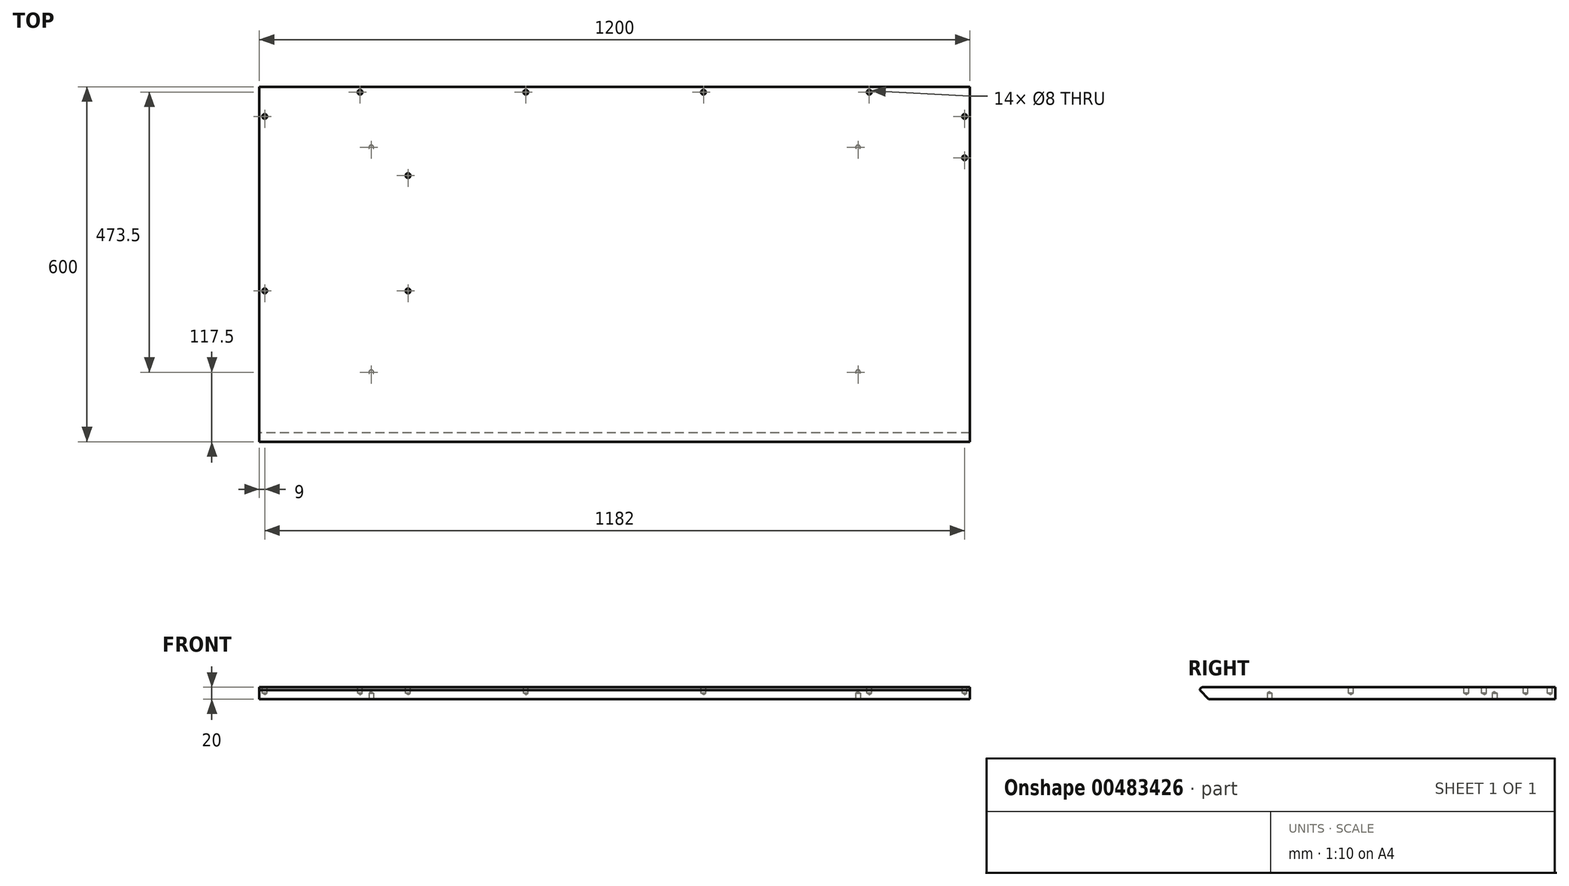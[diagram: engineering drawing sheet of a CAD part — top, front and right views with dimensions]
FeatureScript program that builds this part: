
annotation { "Feature Type Name" : "Feature", "Feature Type Description" : "" }
export const myFeature = defineFeature(function(context is Context, id is Id, definition is map)
    precondition{}
    {
        {
            var Q0;
            Q0=qCreatedBy(makeId("Top.planeOp"),FACE);
            var sketch = newSketch(context, id + "F0", { "sketchPlane" : qUnion([Q0])});
            skLineSegment(sketch, "E0.bottom", {"start": v(0, 0) * mm, "end": v(1200, 0) * mm});
            skLineSegment(sketch, "E0.top", {"start": v(0, -600) * mm, "end": v(1200, -600) * mm});
            skLineSegment(sketch, "E0.left", {"start": v(0, 0) * mm, "end": v(0, -600) * mm});
            skLineSegment(sketch, "E0.right", {"start": v(1200, 0) * mm, "end": v(1200, -600) * mm});
            skSolve(sketch);
        }
        {
            var Q0;
            Q0=makeQuery(id+"F0.imprint","IMPRINT",FACE,{"disambiguationData":[TD([[makeQuery(id+"F0.imprint","IMPRINT",EDGE,{"derivedFrom":sQuery(id+"F0.wireOp",EDGE,"E0.bottom")}),-1.0]])]});
            extrude(context, id + "F1", {"entities" : qUnion([Q0]), "depth" : 20 * mm});
        }
        {
            var Q0;
            Q0=makeQuery(id+"F1.opExtrude","CAP_EDGE",EDGE,{"disambiguationData":[OSD([sQuery(id+"F0.wireOp",EDGE,"E0.top")])],"isStart":false});
            fillet(context, id + "F2", {"entities" : qUnion([Q0]), "radius" : 5 * mm, "tangentPropagation" : true, "allowEdgeOverflow" : false});
        }
        {
            var Q0;
            Q0=makeQuery(id+"F1.opExtrude","CAP_EDGE",EDGE,{"disambiguationData":[OSD([sQuery(id+"F0.wireOp",EDGE,"E0.top")])],"isStart":true});
            chamfer(context, id + "F3", {"entities" : qUnion([Q0]), "width" : 15 * mm, "tangentPropagation" : true});
        }
        {
            var Q0;
            Q0=makeQuery(id+"F1.opExtrude","CAP_FACE",FACE,{"disambiguationData":[OSD([sQuery(id+"F0.wireOp",EDGE,"E0.bottom"),sQuery(id+"F0.wireOp",EDGE,"E0.top"),sQuery(id+"F0.wireOp",EDGE,"E0.left"),sQuery(id+"F0.wireOp",EDGE,"E0.right")])],"isStart":false});
            var sketch = newSketch(context, id + "F4", { "sketchPlane" : qUnion([Q0])});
            skPoint(sketch, "E1", {"position": v(1030, -9) * mm});
            skPoint(sketch, "E2", {"position": v(170, -9) * mm});
            skPoint(sketch, "E3", {"position": v(750, -9) * mm});
            skPoint(sketch, "E4", {"position": v(450, -9) * mm});
            skPoint(sketch, "E5", {"position": v(9, -50) * mm});
            skPoint(sketch, "E6", {"position": v(9, -345) * mm});
            skPoint(sketch, "E7", {"position": v(251, -150) * mm});
            skPoint(sketch, "E8", {"position": v(251, -345) * mm});
            skPoint(sketch, "E9", {"position": v(1191, -50) * mm});
            skPoint(sketch, "E10", {"position": v(1191, -120) * mm});
            skSolve(sketch);
        }
        {
            var Q0;
            Q0=makeQuery(id+"F1.opExtrude","CAP_FACE",FACE,{"disambiguationData":[OSD([sQuery(id+"F0.wireOp",EDGE,"E0.bottom"),sQuery(id+"F0.wireOp",EDGE,"E0.top"),sQuery(id+"F0.wireOp",EDGE,"E0.left"),sQuery(id+"F0.wireOp",EDGE,"E0.right")])],"isStart":true});
            var sketch = newSketch(context, id + "F5", { "sketchPlane" : qUnion([Q0])});
            skPoint(sketch, "E11", {"position": v(189, 482.5) * mm});
            skPoint(sketch, "E12", {"position": v(189, 102.5) * mm});
            skPoint(sketch, "E13", {"position": v(1011, 102.5) * mm});
            skPoint(sketch, "E14", {"position": v(1011, 482.5) * mm});
            skSolve(sketch);
        }
        {
            var Q0;
            Q0=sQuery(id+"F4.wireOp",VERTEX,"E1");
            var Q1;
            Q1=sQuery(id+"F4.wireOp",VERTEX,"E3");
            var Q2;
            Q2=sQuery(id+"F4.wireOp",VERTEX,"E4");
            var Q3;
            Q3=sQuery(id+"F4.wireOp",VERTEX,"E2");
            var Q4;
            Q4=sQuery(id+"F4.wireOp",VERTEX,"E5");
            var Q5;
            Q5=sQuery(id+"F4.wireOp",VERTEX,"E6");
            var Q6;
            Q6=sQuery(id+"F4.wireOp",VERTEX,"E7");
            var Q7;
            Q7=sQuery(id+"F4.wireOp",VERTEX,"E8");
            var Q8;
            Q8=sQuery(id+"F4.wireOp",VERTEX,"E10");
            var Q9;
            Q9=sQuery(id+"F4.wireOp",VERTEX,"E9");
            var Q10;
            Q10=sQuery(id+"F5.wireOp",VERTEX,"E11");
            var Q11;
            Q11=sQuery(id+"F5.wireOp",VERTEX,"E12");
            var Q12;
            Q12=sQuery(id+"F5.wireOp",VERTEX,"E13");
            var Q13;
            Q13=sQuery(id+"F5.wireOp",VERTEX,"E14");
            var Q14;
            Q14=makeQuery(id+"F1.opExtrude","SWEPT_BODY",BODY,{"disambiguationData":[OSD([sQuery(id+"F0.wireOp",EDGE,"E0.bottom"),sQuery(id+"F0.wireOp",EDGE,"E0.top"),sQuery(id+"F0.wireOp",EDGE,"E0.left"),sQuery(id+"F0.wireOp",EDGE,"E0.right")])]});
            hole(context, id + "F6", {"style" : HoleStyle.SIMPLE, "endStyle" : HoleEndStyle.BLIND, "standardTappedOrClearance" : lookupTablePath({ "standard" : "ISO", "size" : "8", "type" : "Drilled" }), "standardBlindInLast" : lookupTablePath({ "standard" : "ISO", "size" : "8", "type" : "Drilled" }), "holeDiameter" : 8 * mm, "holeDepth" : 10 * mm, "isTappedThrough" : true, "tappedDepth" : 12 * mm, "tapClearance" : 3, "locations" : qUnion([Q0, Q1, Q2, Q3, Q4, Q5, Q6, Q7, Q8, Q9, Q10, Q11, Q12, Q13]), "scope" : qUnion([Q14])});
        }
    });
